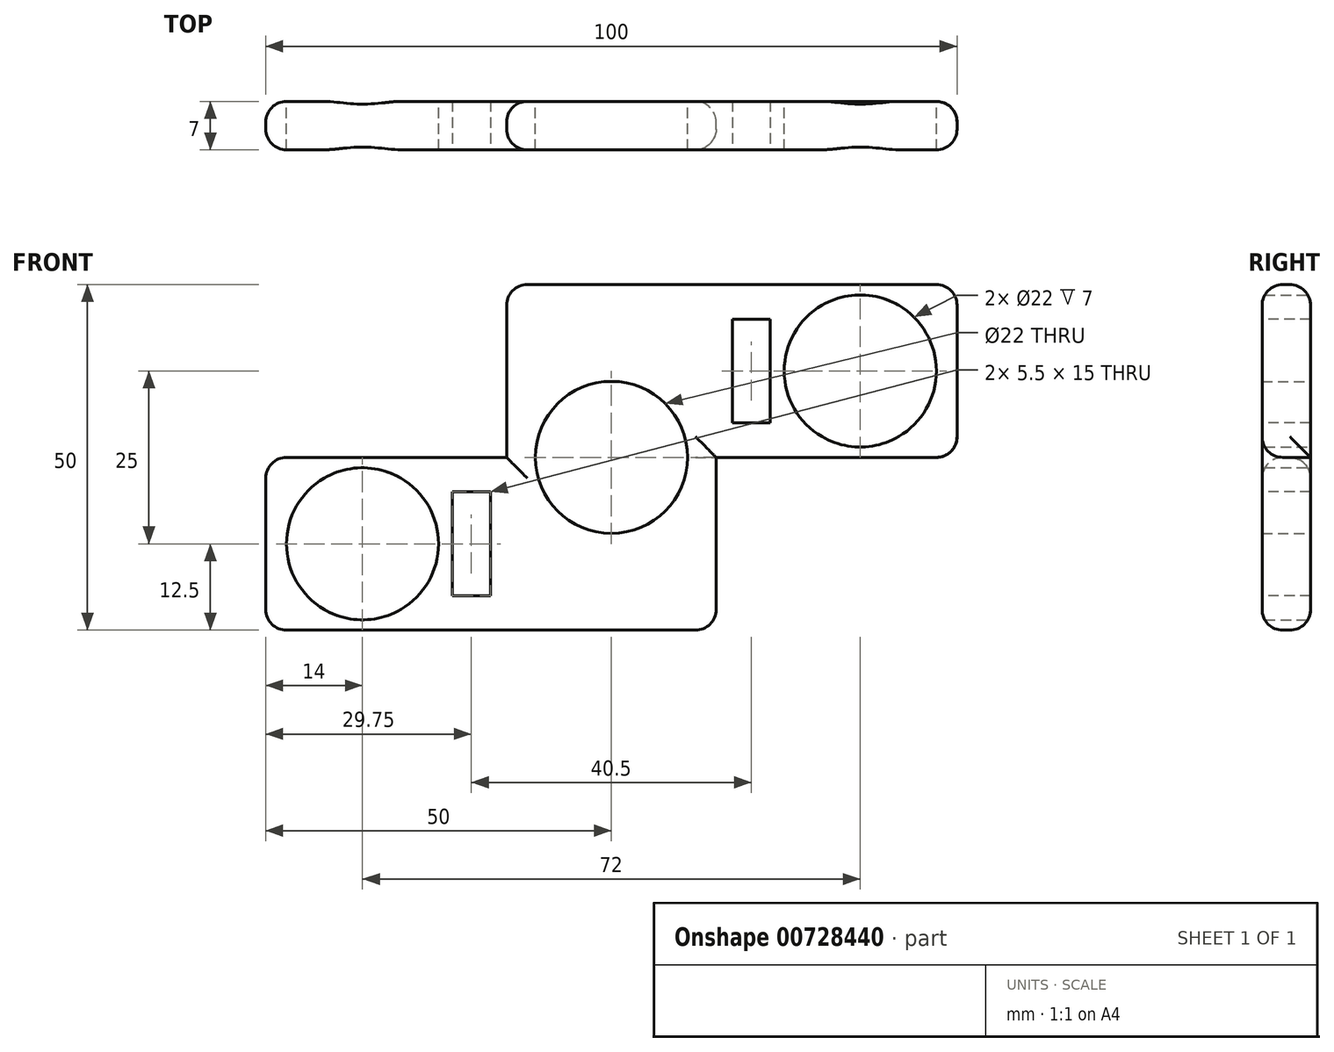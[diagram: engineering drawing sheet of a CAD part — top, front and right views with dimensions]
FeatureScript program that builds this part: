
annotation { "Feature Type Name" : "Feature", "Feature Type Description" : "" }
export const myFeature = defineFeature(function(context is Context, id is Id, definition is map)
    precondition{}
    {
        {
            var Q0;
            Q0=qCreatedBy(makeId("Front.planeOp"),FACE);
            var sketch = newSketch(context, id + "F0", { "sketchPlane" : qUnion([Q0])});
            skCircle(sketch, "E0", {"center": v(0, 0) * mm, "radius": 11 * mm});
            skSolve(sketch);
        }
        {
            var Q0;
            Q0=qCreatedBy(makeId("Front.planeOp"),FACE);
            var sketch = newSketch(context, id + "F1", { "sketchPlane" : qUnion([Q0])});
            skLineSegment(sketch, "E1.bottom", {"start": v(-50, 25) * mm, "end": v(50, 25) * mm});
            skLineSegment(sketch, "E1.top", {"start": v(-50, -25) * mm, "end": v(50, -25) * mm});
            skLineSegment(sketch, "E1.left", {"start": v(-50, 25) * mm, "end": v(-50, -25) * mm});
            skLineSegment(sketch, "E1.right", {"start": v(50, 25) * mm, "end": v(50, -25) * mm});
            skLineSegment(sketch, "E2.bottom", {"start": v(-50, 25) * mm, "end": v(-15.16, 25) * mm});
            skLineSegment(sketch, "E2.top", {"start": v(-50, 0) * mm, "end": v(-15.16, 0) * mm});
            skLineSegment(sketch, "E2.left", {"start": v(-50, 25) * mm, "end": v(-50, 0) * mm});
            skLineSegment(sketch, "E2.right", {"start": v(-15.16, 25) * mm, "end": v(-15.16, 0) * mm});
            skLineSegment(sketch, "E3.bottom", {"start": v(50, -25) * mm, "end": v(15.16, -25) * mm});
            skLineSegment(sketch, "E3.top", {"start": v(50, 0) * mm, "end": v(15.16, 0) * mm});
            skLineSegment(sketch, "E3.left", {"start": v(50, -25) * mm, "end": v(50, 0) * mm});
            skLineSegment(sketch, "E3.right", {"start": v(15.16, -25) * mm, "end": v(15.16, 0) * mm});
            skSolve(sketch);
        }
        {
            var Q0;
            {var subQ7=sQuery(id+"F1.wireOp",EDGE,"E2.top");Q0=makeQuery(id+"F1.imprint","IMPRINT",FACE,{"disambiguationData":[TD([[makeQuery(id+"F1.imprint","IMPRINT",EDGE,{"derivedFrom":subQ7}),-1.0]])]});}
            extrude(context, id + "F2", {"entities" : qUnion([Q0]), "depth" : 7 * mm, "offsetDistance" : 25 * mm});
        }
        {
            var Q0;
            Q0 = qSketchRegion(id + "F0", true);
            extrude(context, id + "F3", {"entities" : qUnion([Q0]), "operationType" : NewBodyOperationType.REMOVE, "endBound" : BoundingType.THROUGH_ALL, "depth" : 25 * mm, "offsetDistance" : 25 * mm});
        }
        {
            var Q0;
            Q0=qCreatedBy(makeId("Front.planeOp"),FACE);
            var sketch = newSketch(context, id + "F4", { "sketchPlane" : qUnion([Q0])});
            skCircle(sketch, "E4", {"center": v(-36, -12.5) * mm, "radius": 11 * mm});
            skCircle(sketch, "E5", {"center": v(36, 12.5) * mm, "radius": 11 * mm});
            skSolve(sketch);
        }
        {
            var Q0;
            Q0 = qSketchRegion(id + "F4", true);
            extrude(context, id + "F5", {"entities" : qUnion([Q0]), "operationType" : NewBodyOperationType.REMOVE, "endBound" : BoundingType.THROUGH_ALL, "depth" : 25 * mm, "offsetDistance" : 25 * mm});
        }
        {
            var Q0;
            Q0=makeQuery(id+"F2.opExtrude","CAP_EDGE",EDGE,{"disambiguationData":[OSD([sQuery(id+"F1.wireOp",EDGE,"E2.top")])],"isStart":false});
            var Q1;
            Q1=makeQuery(id+"F2.opExtrude","CAP_EDGE",EDGE,{"disambiguationData":[OSD([sQuery(id+"F1.wireOp",EDGE,"E2.top")])],"isStart":true});
            fillet(context, id + "F6", {"entities" : qUnion([Q0, Q1]), "radius" : 3 * mm, "tangentPropagation" : true, "allowEdgeOverflow" : false});
        }
        {
            var Q0;
            Q0=makeQuery(id+"F2.opExtrude","CAP_EDGE",EDGE,{"disambiguationData":[OSD([sQuery(id+"F1.wireOp",EDGE,"E1.top")])],"isStart":false});
            var Q1;
            Q1=makeQuery(id+"F2.opExtrude","CAP_EDGE",EDGE,{"disambiguationData":[OSD([sQuery(id+"F1.wireOp",EDGE,"E1.top")])],"isStart":true});
            fillet(context, id + "F7", {"entities" : qUnion([Q0, Q1]), "radius" : 3 * mm, "tangentPropagation" : true, "allowEdgeOverflow" : false});
        }
        {
            var Q0;
            Q0=makeQuery(id+"F2.opExtrude","CAP_EDGE",EDGE,{"disambiguationData":[OSD([sQuery(id+"F1.wireOp",EDGE,"E2.right")])],"isStart":false});
            var Q1;
            Q1=makeQuery(id+"F2.opExtrude","CAP_EDGE",EDGE,{"disambiguationData":[OSD([sQuery(id+"F1.wireOp",EDGE,"E2.right")])],"isStart":true});
            fillet(context, id + "F8", {"entities" : qUnion([Q0, Q1]), "radius" : 3 * mm, "tangentPropagation" : true, "allowEdgeOverflow" : false});
        }
        {
            var Q0;
            Q0=makeQuery(id+"F2.opExtrude","CAP_EDGE",EDGE,{"disambiguationData":[OSD([sQuery(id+"F1.wireOp",EDGE,"E3.right")])],"isStart":false});
            var Q1;
            Q1=makeQuery(id+"F2.opExtrude","CAP_EDGE",EDGE,{"disambiguationData":[OSD([sQuery(id+"F1.wireOp",EDGE,"E3.right")])],"isStart":true});
            fillet(context, id + "F9", {"entities" : qUnion([Q0, Q1]), "radius" : 3 * mm, "tangentPropagation" : true, "allowEdgeOverflow" : false});
        }
        {
            var Q0;
            Q0=makeQuery(id+"F2.opExtrude","CAP_EDGE",EDGE,{"disambiguationData":[OSD([sQuery(id+"F1.wireOp",EDGE,"E3.top")])],"isStart":false});
            fillet(context, id + "F10", {"entities" : qUnion([Q0]), "radius" : 3 * mm, "tangentPropagation" : true, "allowEdgeOverflow" : false});
        }
        {
            var Q0;
            Q0=makeQuery(id+"F2.opExtrude","CAP_EDGE",EDGE,{"disambiguationData":[OSD([sQuery(id+"F1.wireOp",EDGE,"E1.bottom")])],"isStart":false});
            var Q1;
            Q1=makeQuery(id+"F2.opExtrude","CAP_EDGE",EDGE,{"disambiguationData":[OSD([sQuery(id+"F1.wireOp",EDGE,"E1.bottom")])],"isStart":true});
            fillet(context, id + "F11", {"entities" : qUnion([Q0, Q1]), "radius" : 3 * mm, "tangentPropagation" : true, "allowEdgeOverflow" : false});
        }
        {
            var Q0;
            Q0=makeQuery(id+"F2.opExtrude","CAP_EDGE",EDGE,{"disambiguationData":[OSD([sQuery(id+"F1.wireOp",EDGE,"E1.right")])],"isStart":false});
            var Q1;
            Q1=makeQuery(id+"F2.opExtrude","SWEPT_FACE",FACE,{"disambiguationData":[OSD([sQuery(id+"F1.wireOp",EDGE,"E1.right")])]});
            fillet(context, id + "F12", {"entities" : qUnion([Q0, Q1]), "radius" : 3 * mm, "tangentPropagation" : true, "allowEdgeOverflow" : false});
        }
        {
            var Q0;
            Q0=makeQuery(id+"F2.opExtrude","SWEPT_FACE",FACE,{"disambiguationData":[OSD([sQuery(id+"F1.wireOp",EDGE,"E1.left")])]});
            fillet(context, id + "F13", {"entities" : qUnion([Q0]), "radius" : 3 * mm, "tangentPropagation" : true, "allowEdgeOverflow" : false});
        }
        {
            var Q0;
            Q0=makeQuery(id+"F11.opFillet","SPLIT",FACE,{"disambiguationData":[OD(0.0)],"derivedFrom":makeQuery(id+"F7.opFillet","SPLIT",FACE,{"disambiguationData":[OD(0.0)],"derivedFrom":makeQuery(id+"F2.opExtrude","CAP_FACE",FACE,{"disambiguationData":[OSD([sQuery(id+"F1.wireOp",EDGE,"E1.bottom"),sQuery(id+"F1.wireOp",EDGE,"E1.top"),sQuery(id+"F1.wireOp",EDGE,"E1.left"),sQuery(id+"F1.wireOp",EDGE,"E1.right"),sQuery(id+"F1.wireOp",EDGE,"E2.top"),sQuery(id+"F1.wireOp",EDGE,"E2.right"),sQuery(id+"F1.wireOp",EDGE,"E3.top"),sQuery(id+"F1.wireOp",EDGE,"E3.right")])],"isStart":false})})});
            var sketch = newSketch(context, id + "F14", { "sketchPlane" : qUnion([Q0])});
            skLineSegment(sketch, "E6.bottom", {"start": v(23, 5) * mm, "end": v(17.5, 5) * mm});
            skLineSegment(sketch, "E6.top", {"start": v(23, 20) * mm, "end": v(17.5, 20) * mm});
            skLineSegment(sketch, "E6.left", {"start": v(23, 5) * mm, "end": v(23, 20) * mm});
            skLineSegment(sketch, "E6.right", {"start": v(17.5, 5) * mm, "end": v(17.5, 20) * mm});
            skSolve(sketch);
        }
        {
            var Q0;
            Q0=makeQuery(id+"F14.imprint","IMPRINT",FACE,{"disambiguationData":[TD([[makeQuery(id+"F14.imprint","IMPRINT",EDGE,{"derivedFrom":sQuery(id+"F14.wireOp",EDGE,"E6.bottom")}),1.0]])]});
            var sketch = newSketch(context, id + "F15", { "sketchPlane" : qUnion([Q0])});
            skLineSegment(sketch, "E7.bottom", {"start": v(-23, -20) * mm, "end": v(-17.5, -20) * mm});
            skLineSegment(sketch, "E7.top", {"start": v(-23, -5) * mm, "end": v(-17.5, -5) * mm});
            skLineSegment(sketch, "E7.left", {"start": v(-23, -20) * mm, "end": v(-23, -5) * mm});
            skLineSegment(sketch, "E7.right", {"start": v(-17.5, -20) * mm, "end": v(-17.5, -5) * mm});
            skSolve(sketch);
        }
        {
            var Q0;
            Q0 = qSketchRegion(id + "F15", true);
            extrude(context, id + "F16", {"entities" : qUnion([Q0]), "operationType" : NewBodyOperationType.REMOVE, "endBound" : BoundingType.THROUGH_ALL, "oppositeDirection" : true, "depth" : 25 * mm, "offsetDistance" : 25 * mm});
        }
        {
            var Q0;
            Q0 = qSketchRegion(id + "F14", true);
            extrude(context, id + "F17", {"entities" : qUnion([Q0]), "operationType" : NewBodyOperationType.REMOVE, "endBound" : BoundingType.THROUGH_ALL, "oppositeDirection" : true, "depth" : 25 * mm, "offsetDistance" : 25 * mm});
        }
    });
